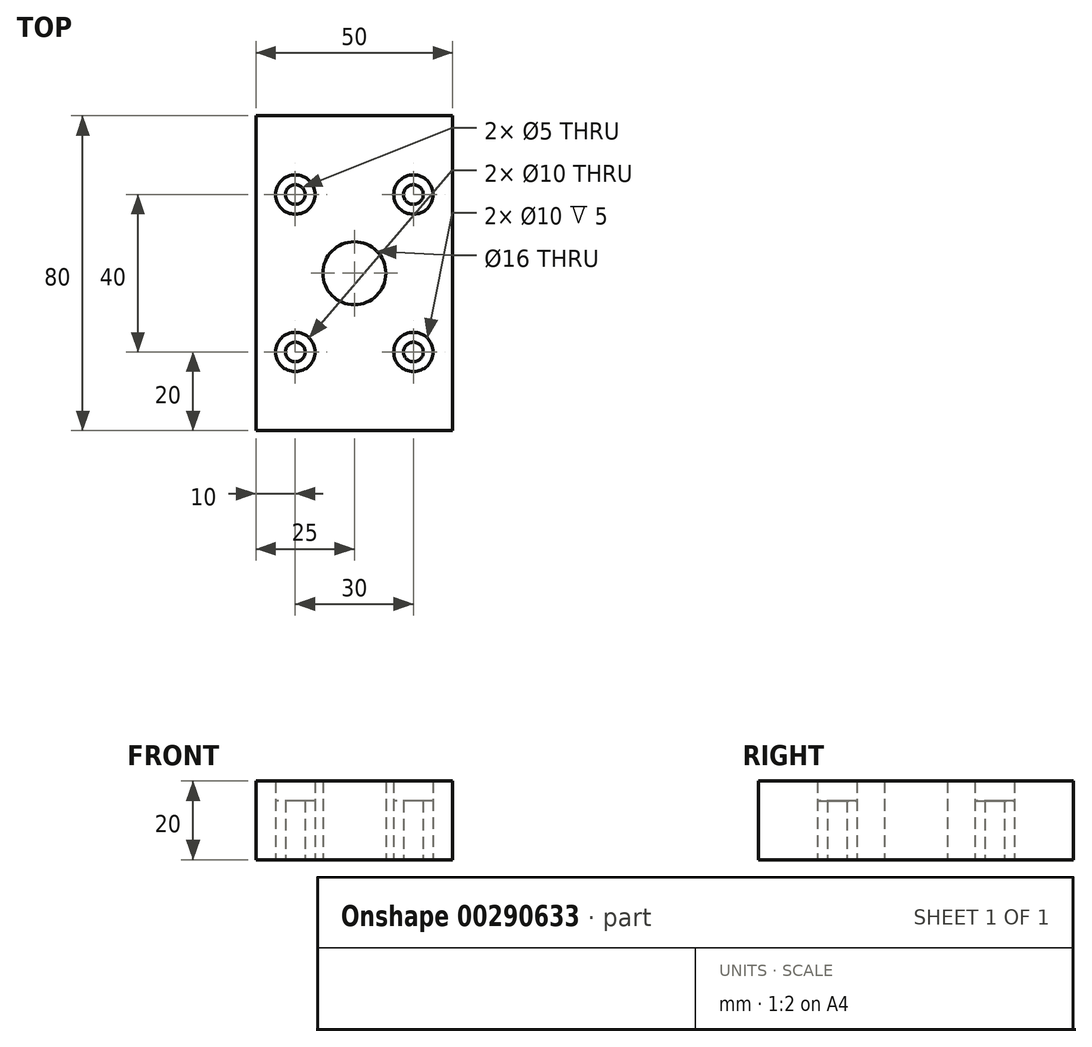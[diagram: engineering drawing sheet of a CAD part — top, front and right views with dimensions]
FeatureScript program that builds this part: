
annotation { "Feature Type Name" : "Feature", "Feature Type Description" : "" }
export const myFeature = defineFeature(function(context is Context, id is Id, definition is map)
    precondition{}
    {
        {
            var Q0;
            Q0=qCreatedBy(makeId("Top.planeOp"),FACE);
            var sketch = newSketch(context, id + "F0", { "sketchPlane" : qUnion([Q0])});
            skCircle(sketch, "E0", {"center": v(0, 0) * mm, "radius": 8 * mm});
            skLineSegment(sketch, "E1.bottom", {"start": v(-25, 40) * mm, "end": v(25, 40) * mm});
            skLineSegment(sketch, "E1.top", {"start": v(-25, -40) * mm, "end": v(25, -40) * mm});
            skLineSegment(sketch, "E1.left", {"start": v(-25, 40) * mm, "end": v(-25, -40) * mm});
            skLineSegment(sketch, "E1.right", {"start": v(25, 40) * mm, "end": v(25, -40) * mm});
            skLineSegment(sketch, "E2", {"start": v(0, 40) * mm, "end": v(0, -40) * mm, "construction": true});
            skPoint(sketch, "E2.endSnap0", {"position": v(0, -40) * mm});
            skLineSegment(sketch, "E3", {"start": v(-25, 20) * mm, "end": v(25, 20) * mm, "construction": true});
            skLineSegment(sketch, "E4", {"start": v(-15, 40) * mm, "end": v(-15, -40) * mm, "construction": true});
            skCircle(sketch, "E5", {"center": v(-15, 20) * mm, "radius": 2.5 * mm});
            skLineSegment(sketch, "E6", {"start": v(-25, 0) * mm, "end": v(25, 0) * mm, "construction": true});
            skLineSegment(sketch, "E7", {"start": v(-25, -20) * mm, "end": v(25, -20) * mm, "construction": true});
            skCircle(sketch, "E8.MirrorC", {"center": v(15, 20) * mm, "radius": 2.5 * mm});
            skLineSegment(sketch, "E9.MirrorCS", {"start": v(25, 20) * mm, "end": v(-25, 20) * mm, "construction": true});
            skCircle(sketch, "E10.MirrorC", {"center": v(-15, -20) * mm, "radius": 2.5 * mm});
            skCircle(sketch, "E11.MirrorC", {"center": v(15, -20) * mm, "radius": 2.5 * mm});
            skCircle(sketch, "E12", {"center": v(-15, 20) * mm, "radius": 5 * mm});
            skCircle(sketch, "E13.MirrorC", {"center": v(15, 20) * mm, "radius": 5 * mm});
            skCircle(sketch, "E14.MirrorC", {"center": v(-15, -20) * mm, "radius": 5 * mm});
            skCircle(sketch, "E15.MirrorC", {"center": v(15, -20) * mm, "radius": 5 * mm});
            skSolve(sketch);
        }
        {
            var Q0;
            Q0 = qSketchRegion(id + "F0", true);
            var Q1;
            Q1=makeQuery(id+"F0.imprint","IMPRINT",FACE,{"disambiguationData":[TD([[makeQuery(id+"F0.imprint","IMPRINT",EDGE,{"derivedFrom":sQuery(id+"F0.wireOp",EDGE,"E5")}),-1.0]])]});
            var Q2;
            Q2=makeQuery(id+"F0.imprint","IMPRINT",FACE,{"disambiguationData":[TD([[makeQuery(id+"F0.imprint","IMPRINT",EDGE,{"derivedFrom":sQuery(id+"F0.wireOp",EDGE,"E8.MirrorC")}),1.0]])]});
            var Q3;
            Q3=makeQuery(id+"F0.imprint","IMPRINT",FACE,{"disambiguationData":[TD([[makeQuery(id+"F0.imprint","IMPRINT",EDGE,{"derivedFrom":sQuery(id+"F0.wireOp",EDGE,"E11.MirrorC")}),-1.0]])]});
            var Q4;
            Q4=makeQuery(id+"F0.imprint","IMPRINT",FACE,{"disambiguationData":[TD([[makeQuery(id+"F0.imprint","IMPRINT",EDGE,{"derivedFrom":sQuery(id+"F0.wireOp",EDGE,"E10.MirrorC")}),1.0]])]});
            extrude(context, id + "F1", {"entities" : qUnion([Q0, Q1, Q2, Q3, Q4]), "depth" : 20 * mm});
        }
        {
            var Q0;
            Q0=makeQuery(id+"F0.imprint","IMPRINT",FACE,{"disambiguationData":[TD([[makeQuery(id+"F0.imprint","IMPRINT",EDGE,{"derivedFrom":sQuery(id+"F0.wireOp",EDGE,"E10.MirrorC")}),1.0]])]});
            var Q1;
            Q1=makeQuery(id+"F0.imprint","IMPRINT",FACE,{"disambiguationData":[TD([[makeQuery(id+"F0.imprint","IMPRINT",EDGE,{"derivedFrom":sQuery(id+"F0.wireOp",EDGE,"E11.MirrorC")}),-1.0]])]});
            var Q2;
            Q2=makeQuery(id+"F0.imprint","IMPRINT",FACE,{"disambiguationData":[TD([[makeQuery(id+"F0.imprint","IMPRINT",EDGE,{"derivedFrom":sQuery(id+"F0.wireOp",EDGE,"E5")}),-1.0]])]});
            var Q3;
            Q3=makeQuery(id+"F0.imprint","IMPRINT",FACE,{"disambiguationData":[TD([[makeQuery(id+"F0.imprint","IMPRINT",EDGE,{"derivedFrom":sQuery(id+"F0.wireOp",EDGE,"E8.MirrorC")}),1.0]])]});
            extrude(context, id + "F2", {"entities" : qUnion([Q0, Q1, Q2, Q3]), "operationType" : NewBodyOperationType.REMOVE, "depth" : 20 * mm, "hasSecondDirection" : true, "secondDirectionOppositeDirection" : false, "secondDirectionDepth" : 15 * mm});
        }
    });
